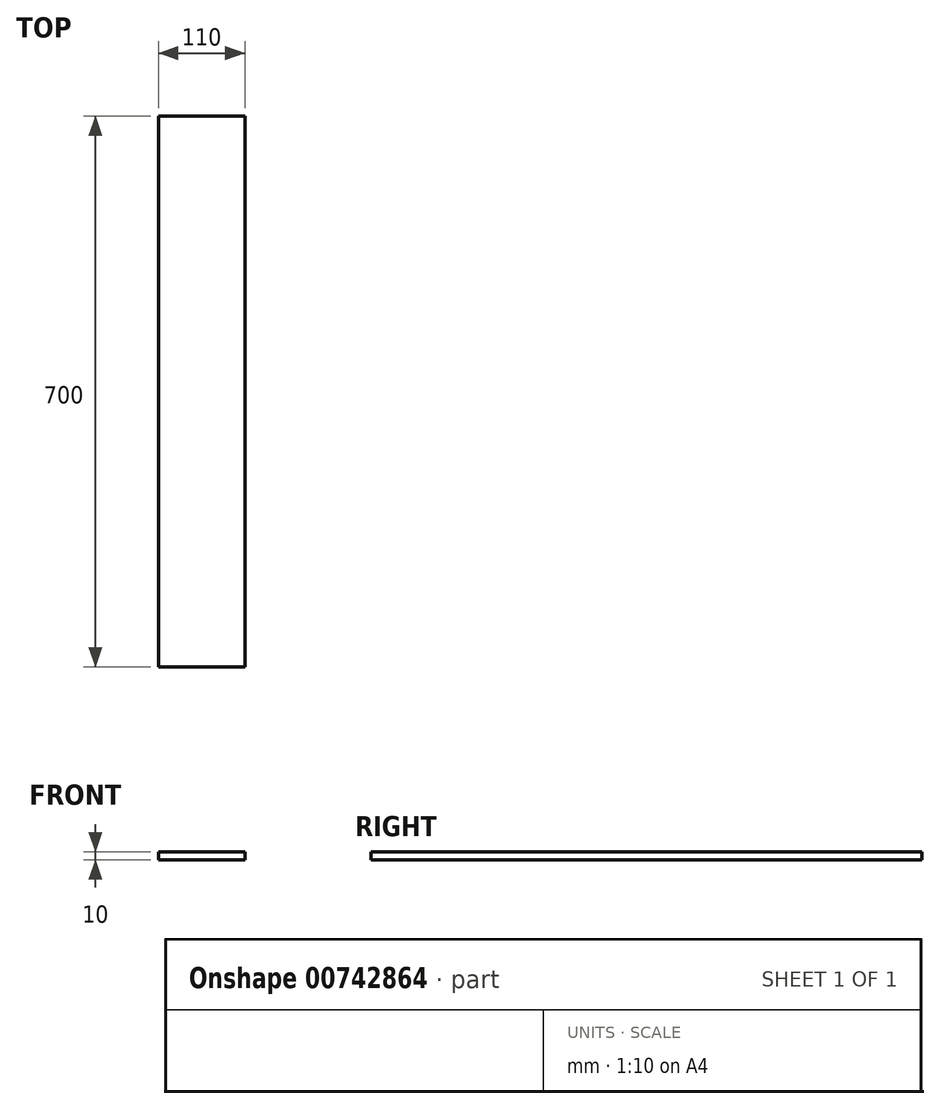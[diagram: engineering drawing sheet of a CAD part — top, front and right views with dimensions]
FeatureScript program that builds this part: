
annotation { "Feature Type Name" : "Feature", "Feature Type Description" : "" }
export const myFeature = defineFeature(function(context is Context, id is Id, definition is map)
    precondition{}
    {
        {
            var Q0;
            Q0=qCreatedBy(makeId("Top.planeOp"),FACE);
            var sketch = newSketch(context, id + "F0", { "sketchPlane" : qUnion([Q0])});
            skLineSegment(sketch, "E0.bottom", {"start": v(55, 350) * mm, "end": v(-55, 350) * mm});
            skLineSegment(sketch, "E0.top", {"start": v(55, -350) * mm, "end": v(-55, -350) * mm});
            skLineSegment(sketch, "E0.left", {"start": v(55, 350) * mm, "end": v(55, -350) * mm});
            skLineSegment(sketch, "E0.right", {"start": v(-55, 350) * mm, "end": v(-55, -350) * mm});
            skPoint(sketch, "E0.middle", {"position": v(0, 0) * mm});
            skSolve(sketch);
        }
        {
            var Q0;
            Q0 = qSketchRegion(id + "F0", true);
            extrude(context, id + "F1", {"entities" : qUnion([Q0]), "endBound" : BoundingType.SYMMETRIC, "depth" : 10 * mm, "offsetDistance" : 25.4 * mm});
        }
    });
